# Revit family: Domotics-DomesticRanges-GEWISS-SYSTEM_POWER-SOCKET-OUTLET_ARG
name_source: partatom
category: Apparecchi elettrici
revit_build: Autodesk Revit 2016 (Build: 20161004_0715(x64)
units: mm (PartAtom-declared; Revit-internal decimal feet)

## family parameters
Condiviso = Sì
Host = Superficie
Mantenere orientamento annotazione = Sì
Punto di calcolo locali = Sì
Quota connettore circolare = Usa diametro
Taglio con vuoti quando caricato = Sì
Tipo di parte = Normale

## types (2) — shared parameters
Carico apparente = 0 VA
Catalogue = DOMOTICS
Catalogue Range = SYSTEM - DOMESTIC RANGE
Description. = Argentina
Description: = 2P+E - 10A
Electrocod = 0131
For plug pins = Flat
IDF = e444df49-3182-48a5-978b-9fa648243107
IDT = 489c1a53-626f-4b13-8bb9-09ec56726b9e
Immagine tipo = GW21248.jpg
N. poli = 1
No. SYSTEM modules = 2
Produttore = GEWISS S.p.A.
Prospetto di default = 1219 mm
SEO = Socket outlet
Standard = Argentinian
Standard: = Argentinian
TIPO = System Prese Argentina_GENERICO : GW21248 Presa 2P+T 10A standard Argentino nero
TXT ELETTRICO = 10
Technical sheet = https://www.gewiss.com
URL = https://www.gewiss.com
Version file RFA = 19.4
Volt = 230 V
Voltage = 250 V ac
Voltage: = 250 V ac

## per-type parameters (varying)
| type | Colour | Descrizione | EAN code | Modello |
| GW21248 - 10A 2P+E argentinian s.-out.black | Black | 10A 2P+E ARGENTINIAN S.-OUT.SY/BK | 8011564128576 | GW21248 |
| GW20248 - 10A 2P+E argentinian s.-out.white | White | 10A 2P+E ARGENTINIAN S.-OUT.SY/WT | 8011564025998 | GW20248 |

## geometry (parser evidence)
native form markers: Sweep x1
no freeform markers — native parametric forms only
